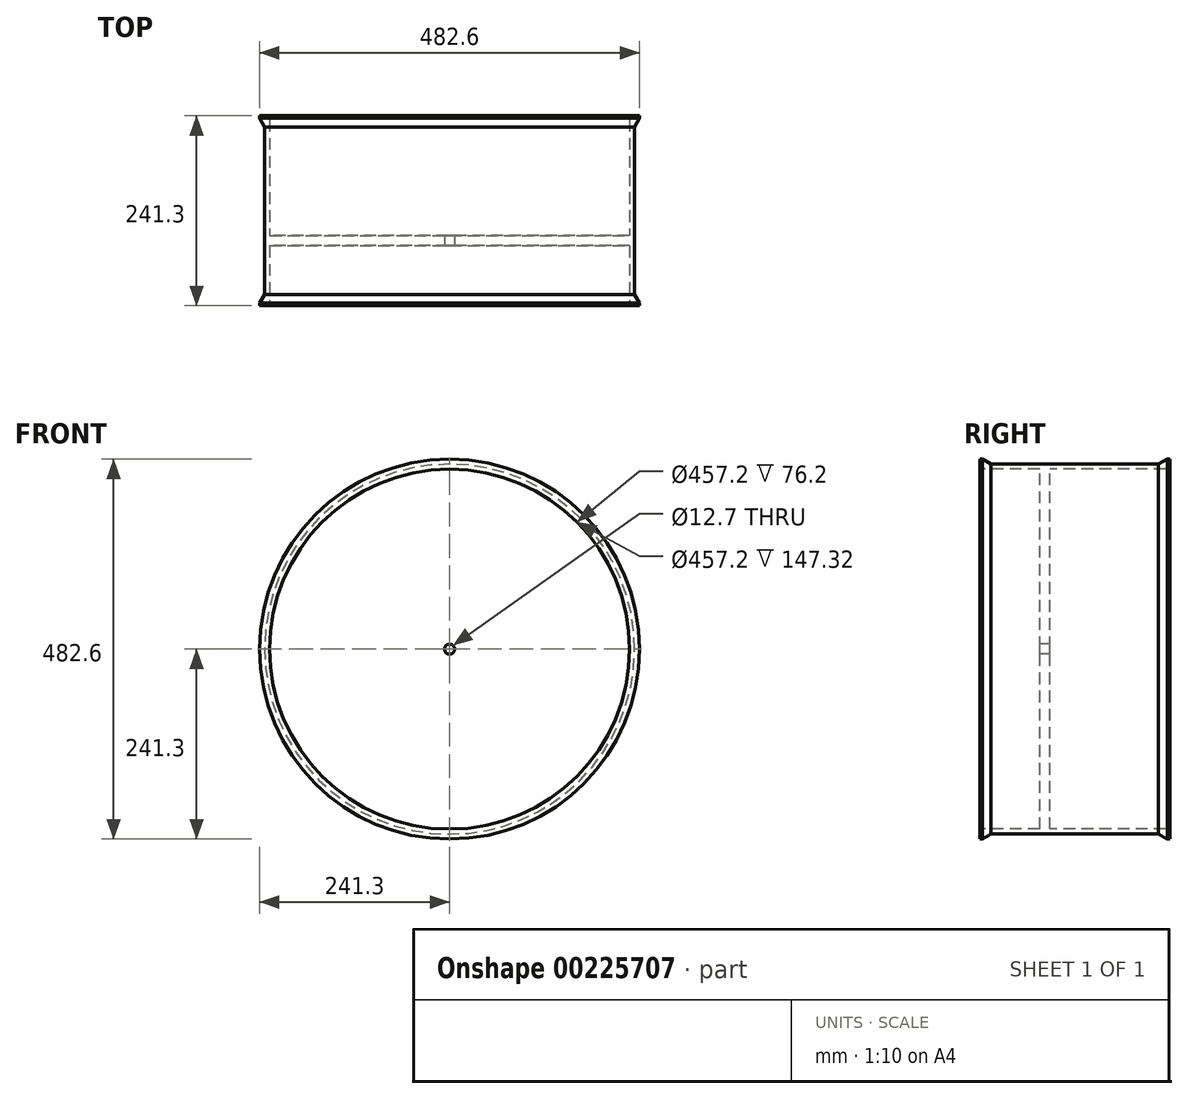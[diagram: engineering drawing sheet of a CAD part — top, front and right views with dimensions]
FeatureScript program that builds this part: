
annotation { "Feature Type Name" : "Feature", "Feature Type Description" : "" }
export const myFeature = defineFeature(function(context is Context, id is Id, definition is map)
    precondition{}
    {
        {
            var Q0;
            Q0=qCreatedBy(makeId("Right.planeOp"),FACE);
            var sketch = newSketch(context, id + "F0", { "sketchPlane" : qUnion([Q0])});
            skLineSegment(sketch, "E0", {"start": v(0, -133.53) * mm, "end": v(0, 88.72) * mm});
            skLineSegment(sketch, "E1", {"start": v(0, 88.72) * mm, "end": v(-76.2, 88.72) * mm});
            skLineSegment(sketch, "E2", {"start": v(-76.2, 88.72) * mm, "end": v(-76.2, 101.42) * mm});
            skLineSegment(sketch, "E3", {"start": v(-76.2, 101.42) * mm, "end": v(-73.03, 101.42) * mm});
            skLineSegment(sketch, "E4", {"start": v(-73.03, 101.42) * mm, "end": v(-62.03, 95.07) * mm});
            skLineSegment(sketch, "E5", {"start": v(-62.03, 95.07) * mm, "end": v(0, 95.07) * mm});
            skLineSegment(sketch, "E6", {"start": v(12.7, 88.72) * mm, "end": v(165.1, 88.72) * mm});
            skLineSegment(sketch, "E7", {"start": v(165.1, 88.72) * mm, "end": v(165.1, 101.42) * mm});
            skLineSegment(sketch, "E8", {"start": v(165.1, 101.42) * mm, "end": v(161.92, 101.42) * mm});
            skLineSegment(sketch, "E9", {"start": v(161.92, 101.42) * mm, "end": v(150.93, 95.07) * mm});
            skLineSegment(sketch, "E10", {"start": v(150.93, 95.07) * mm, "end": v(0, 95.07) * mm});
            skLineSegment(sketch, "E11", {"start": v(12.7, 88.72) * mm, "end": v(12.7, 88.72) * mm});
            skLineSegment(sketch, "E12", {"start": v(0, -133.53) * mm, "end": v(12.7, -133.53) * mm});
            skLineSegment(sketch, "E13", {"start": v(12.7, -133.53) * mm, "end": v(12.7, 88.72) * mm});
            skPoint(sketch, "E14.orphan", {"position": v(24.9, 0) * mm});
            skPoint(sketch, "E15.start.orphan", {"position": v(-12.74, 0) * mm});
            skLineSegment(sketch, "E16", {"start": v(-16.7, -139.88) * mm, "end": v(76.4, -139.88) * mm});
            skSolve(sketch);
        }
        {
            var Q0;
            Q0 = qSketchRegion(id + "F0", true);
            var Q1;
            Q1=sQuery(id+"F0.wireOp",EDGE,"E16");
            revolve(context, id + "F1", {"entities" : qUnion([Q0]), "axis" : qUnion([Q1]), "revolveType" : RevolveType.FULL});
        }
        {
            var Q0;
            Q0=makeQuery(id+"F1.opRevolve","SWEPT_EDGE",EDGE,{"disambiguationData":[OSD([sQuery(id+"F0.wireOp",EDGE,"E6"),sQuery(id+"F0.wireOp",EDGE,"E7")])]});
            fillet(context, id + "F2", {"entities" : qUnion([Q0]), "radius" : 5.08 * mm, "tangentPropagation" : true, "allowEdgeOverflow" : false});
        }
    });
